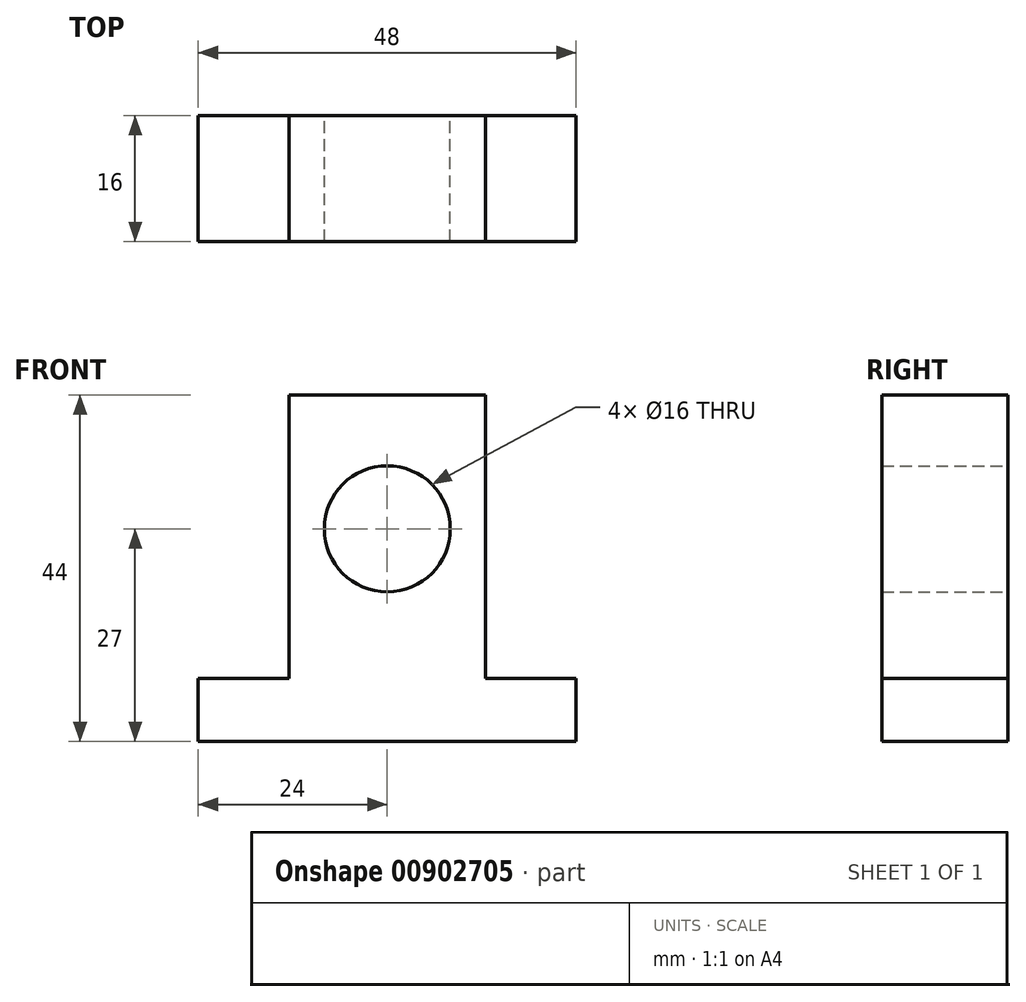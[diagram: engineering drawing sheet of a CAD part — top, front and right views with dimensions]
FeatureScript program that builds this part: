
annotation { "Feature Type Name" : "Feature", "Feature Type Description" : "" }
export const myFeature = defineFeature(function(context is Context, id is Id, definition is map)
    precondition{}
    {
        {
            var Q0;
            Q0=qCreatedBy(makeId("Front.planeOp"),FACE);
            var sketch = newSketch(context, id + "F0", { "sketchPlane" : qUnion([Q0])});
            skCircle(sketch, "E0", {"center": v(0, 27) * mm, "radius": 8 * mm});
            skLineSegment(sketch, "E1.bottom", {"start": v(-12.5, 44) * mm, "end": v(12.5, 44) * mm});
            skLineSegment(sketch, "E1.top", {"start": v(-12.5, 8) * mm, "end": v(12.5, 8) * mm});
            skLineSegment(sketch, "E1.left", {"start": v(-12.5, 44) * mm, "end": v(-12.5, 8) * mm});
            skLineSegment(sketch, "E1.right", {"start": v(12.5, 44) * mm, "end": v(12.5, 8) * mm});
            skLineSegment(sketch, "E2.bottom", {"start": v(-24, 0) * mm, "end": v(24, 0) * mm});
            skLineSegment(sketch, "E2.top", {"start": v(-24, 8) * mm, "end": v(24, 8) * mm});
            skLineSegment(sketch, "E2.left", {"start": v(-24, 0) * mm, "end": v(-24, 8) * mm});
            skLineSegment(sketch, "E2.right", {"start": v(24, 0) * mm, "end": v(24, 8) * mm});
            skPoint(sketch, "E3", {"position": v(0, 44) * mm});
            skLineSegment(sketch, "E4", {"start": v(0, 44) * mm, "end": v(0, 0) * mm, "construction": true});
            skSolve(sketch);
        }
        {
            var Q0;
            {var subQ1=sQuery(id+"F0.wireOp",EDGE,"E1.top");var subQ2=makeQuery(id+"F0.imprint","IMPRINT",EDGE,{"derivedFrom":subQ1});Q0=qUnion([makeQuery(id+"F0.imprint","IMPRINT",FACE,{"disambiguationData":[TD([[subQ2,-1.0]])]}),makeQuery(id+"F0.imprint","IMPRINT",FACE,{"disambiguationData":[TD([[makeQuery(id+"F0.imprint","IMPRINT",EDGE,{"derivedFrom":sQuery(id+"F0.wireOp",EDGE,"E0")}),-1.0]])]})]);}
            extrude(context, id + "F1", {"entities" : qUnion([Q0]), "depth" : 16 * mm, "offsetDistance" : 25 * mm});
        }
    });
